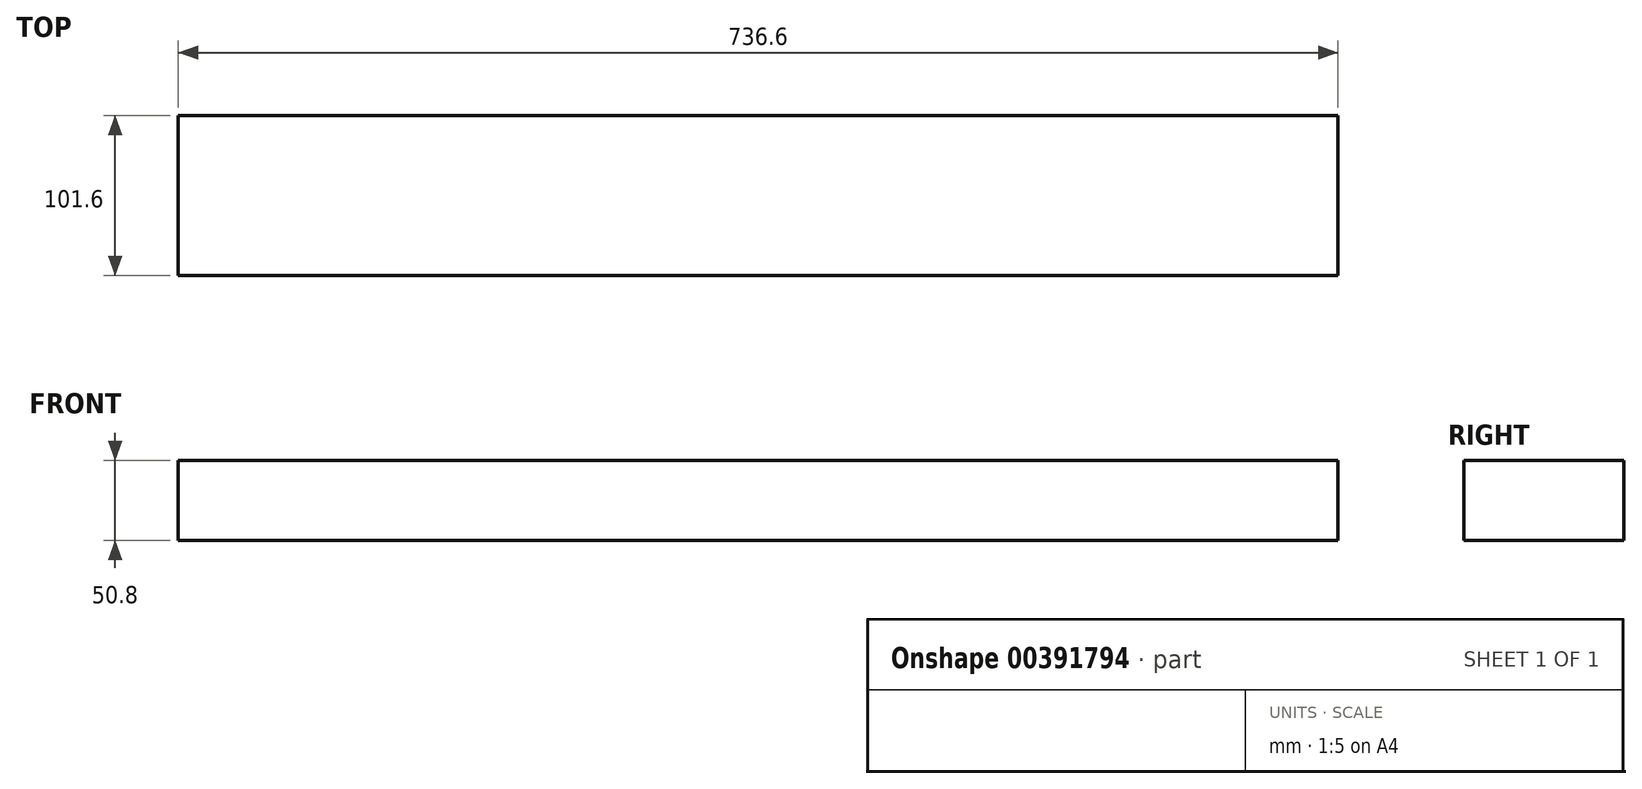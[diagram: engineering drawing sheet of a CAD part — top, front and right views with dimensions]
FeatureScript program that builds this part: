
annotation { "Feature Type Name" : "Feature", "Feature Type Description" : "" }
export const myFeature = defineFeature(function(context is Context, id is Id, definition is map)
    precondition{}
    {
        {
            var Q0;
            Q0=qCreatedBy(makeId("Right.planeOp"),FACE);
            var sketch = newSketch(context, id + "F0", { "sketchPlane" : qUnion([Q0])});
            skLineSegment(sketch, "E0.bottom", {"start": v(0, 0) * mm, "end": v(101.6, 0) * mm});
            skLineSegment(sketch, "E0.top", {"start": v(0, 50.8) * mm, "end": v(101.6, 50.8) * mm});
            skLineSegment(sketch, "E0.left", {"start": v(0, 0) * mm, "end": v(0, 50.8) * mm});
            skLineSegment(sketch, "E0.right", {"start": v(101.6, 0) * mm, "end": v(101.6, 50.8) * mm});
            skSolve(sketch);
        }
        {
            var Q0;
            Q0 = qSketchRegion(id + "F0", true);
            extrude(context, id + "F1", {"entities" : qUnion([Q0]), "depth" : 736.6 * mm});
        }
    });
